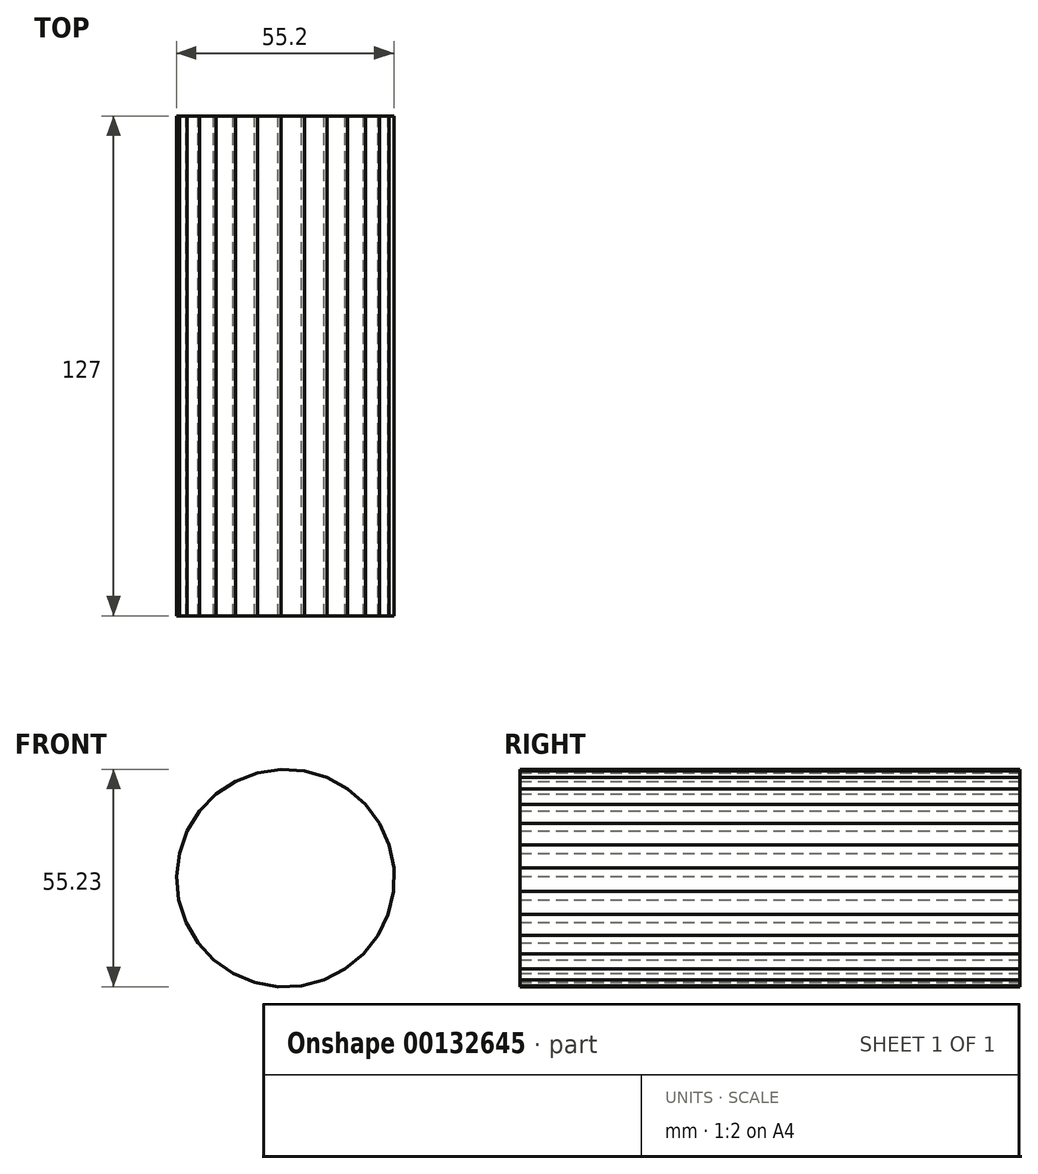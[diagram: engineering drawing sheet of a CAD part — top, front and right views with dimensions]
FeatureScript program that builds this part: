
annotation { "Feature Type Name" : "Feature", "Feature Type Description" : "" }
export const myFeature = defineFeature(function(context is Context, id is Id, definition is map)
    precondition{}
    {
        {
            var Q0;
            Q0=qCreatedBy(makeId("Front.planeOp"),FACE);
            var sketch = newSketch(context, id + "F0", { "sketchPlane" : qUnion([Q0])});
            skCircle(sketch, "E0.cCircle", {"center": v(0, 0) * mm, "radius": 27.5 * mm, "construction": true});
            skLineSegment(sketch, "E0.0", {"start": v(-22.25, -16.43) * mm, "end": v(-25.26, -11.26) * mm});
            skLineSegment(sketch, "E0.1", {"start": v(-25.26, -11.26) * mm, "end": v(-27.1, -5.56) * mm});
            skLineSegment(sketch, "E0.2", {"start": v(-27.1, -5.56) * mm, "end": v(-27.66, 0.39) * mm});
            skLineSegment(sketch, "E0.3", {"start": v(-27.66, 0.39) * mm, "end": v(-26.93, 6.33) * mm});
            skLineSegment(sketch, "E0.4", {"start": v(-26.93, 6.33) * mm, "end": v(-24.94, 11.97) * mm});
            skLineSegment(sketch, "E0.5", {"start": v(-24.94, 11.97) * mm, "end": v(-21.78, 17.05) * mm});
            skLineSegment(sketch, "E0.6", {"start": v(-21.78, 17.05) * mm, "end": v(-17.6, 21.33) * mm});
            skLineSegment(sketch, "E0.7", {"start": v(-17.6, 21.33) * mm, "end": v(-12.6, 24.62) * mm});
            skLineSegment(sketch, "E0.8", {"start": v(-12.6, 24.62) * mm, "end": v(-7.02, 26.75) * mm});
            skLineSegment(sketch, "E0.9", {"start": v(-7.02, 26.75) * mm, "end": v(-1.1, 27.64) * mm});
            skLineSegment(sketch, "E0.10", {"start": v(-1.1, 27.64) * mm, "end": v(4.86, 27.23) * mm});
            skLineSegment(sketch, "E0.11", {"start": v(4.86, 27.23) * mm, "end": v(10.6, 25.55) * mm});
            skLineSegment(sketch, "E0.12", {"start": v(10.6, 25.55) * mm, "end": v(15.84, 22.67) * mm});
            skLineSegment(sketch, "E0.13", {"start": v(15.84, 22.67) * mm, "end": v(20.35, 18.74) * mm});
            skLineSegment(sketch, "E0.14", {"start": v(20.35, 18.74) * mm, "end": v(23.9, 13.92) * mm});
            skLineSegment(sketch, "E0.15", {"start": v(23.9, 13.92) * mm, "end": v(26.33, 8.46) * mm});
            skLineSegment(sketch, "E0.16", {"start": v(26.33, 8.46) * mm, "end": v(27.54, 2.6) * mm});
            skLineSegment(sketch, "E0.17", {"start": v(27.54, 2.6) * mm, "end": v(27.45, -3.38) * mm});
            skLineSegment(sketch, "E0.18", {"start": v(27.45, -3.38) * mm, "end": v(26.08, -9.2) * mm});
            skLineSegment(sketch, "E0.19", {"start": v(26.08, -9.2) * mm, "end": v(23.5, -14.6) * mm});
            skLineSegment(sketch, "E0.20", {"start": v(23.5, -14.6) * mm, "end": v(19.8, -19.3) * mm});
            skLineSegment(sketch, "E0.21", {"start": v(19.8, -19.3) * mm, "end": v(15.2, -23.1) * mm});
            skLineSegment(sketch, "E0.22", {"start": v(15.2, -23.1) * mm, "end": v(9.87, -25.84) * mm});
            skLineSegment(sketch, "E0.23", {"start": v(9.87, -25.84) * mm, "end": v(4.09, -27.35) * mm});
            skLineSegment(sketch, "E0.24", {"start": v(4.09, -27.35) * mm, "end": v(-1.89, -27.6) * mm});
            skLineSegment(sketch, "E0.25", {"start": v(-1.89, -27.6) * mm, "end": v(-7.77, -26.54) * mm});
            skLineSegment(sketch, "E0.26", {"start": v(-7.77, -26.54) * mm, "end": v(-13.3, -24.25) * mm});
            skLineSegment(sketch, "E0.27", {"start": v(-13.3, -24.25) * mm, "end": v(-18.2, -20.83) * mm});
            skLineSegment(sketch, "E0.28", {"start": v(-18.2, -20.83) * mm, "end": v(-22.25, -16.43) * mm});
            skPoint(sketch, "E0.0.midPoint", {"position": v(-23.76, -13.84) * mm});
            skSolve(sketch);
        }
        {
            var Q0;
            Q0=makeQuery(id+"F0.imprint","IMPRINT",FACE,{"disambiguationData":[TD([[makeQuery(id+"F0.imprint","IMPRINT",EDGE,{"derivedFrom":sQuery(id+"F0.wireOp",EDGE,"E0.0")}),-1.0]])]});
            extrude(context, id + "F1", {"entities" : qUnion([Q0]), "endBound" : BoundingType.SYMMETRIC, "depth" : 127 * mm});
        }
    });
